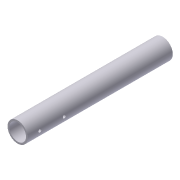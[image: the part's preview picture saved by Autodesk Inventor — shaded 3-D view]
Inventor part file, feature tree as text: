
AUTODESK INVENTOR PART (.ipt)
format: ipt  version: 2012 (Build 160160000, 160)  size: 83,968 bytes
history: native  units: in
note: dims shown in document units (in); Inventor stores cm internally (conversion verified against a paired STEP export)
features: extrude x2, sketch x2, plane x1, pattern_linear x1, other x1, projected_geometry x1
ambient origin geometry x8: Origin, YZ Plane, XZ Plane, XY Plane, X Axis, Y Axis, Z Axis, Center Point
bodies: Solid1 (feature_tree)
feature tree (8):
  extrude  "Extrusion1"  Depth=1.375in
  plane  "Work Plane2"
  extrude  "Extrusion3"  TaperAngle=0.0deg  [1 undecoded]
  pattern_linear  "Rectangular Pattern1"  Spacing1=0.25in  [1 undecoded]
  sketch  "Sketch1"  dims[d0=1.656in d1=1.375in]
  other  "Work Axis2"
  sketch  "Sketch3"  dims[d2=11.875in d3=0.0in d9=0.0in d10=0.25in d11=1.0in d12=15.0in d13=0.0in d14=0.7874in d16=2.0in]
  projected_geometry  "Projected Loop2"
note: 2 required parameter values undecoded (feature->parameter linkage not recoverable at this tier; creation-order binding heuristic only, values carry confidence <= 0.55)
